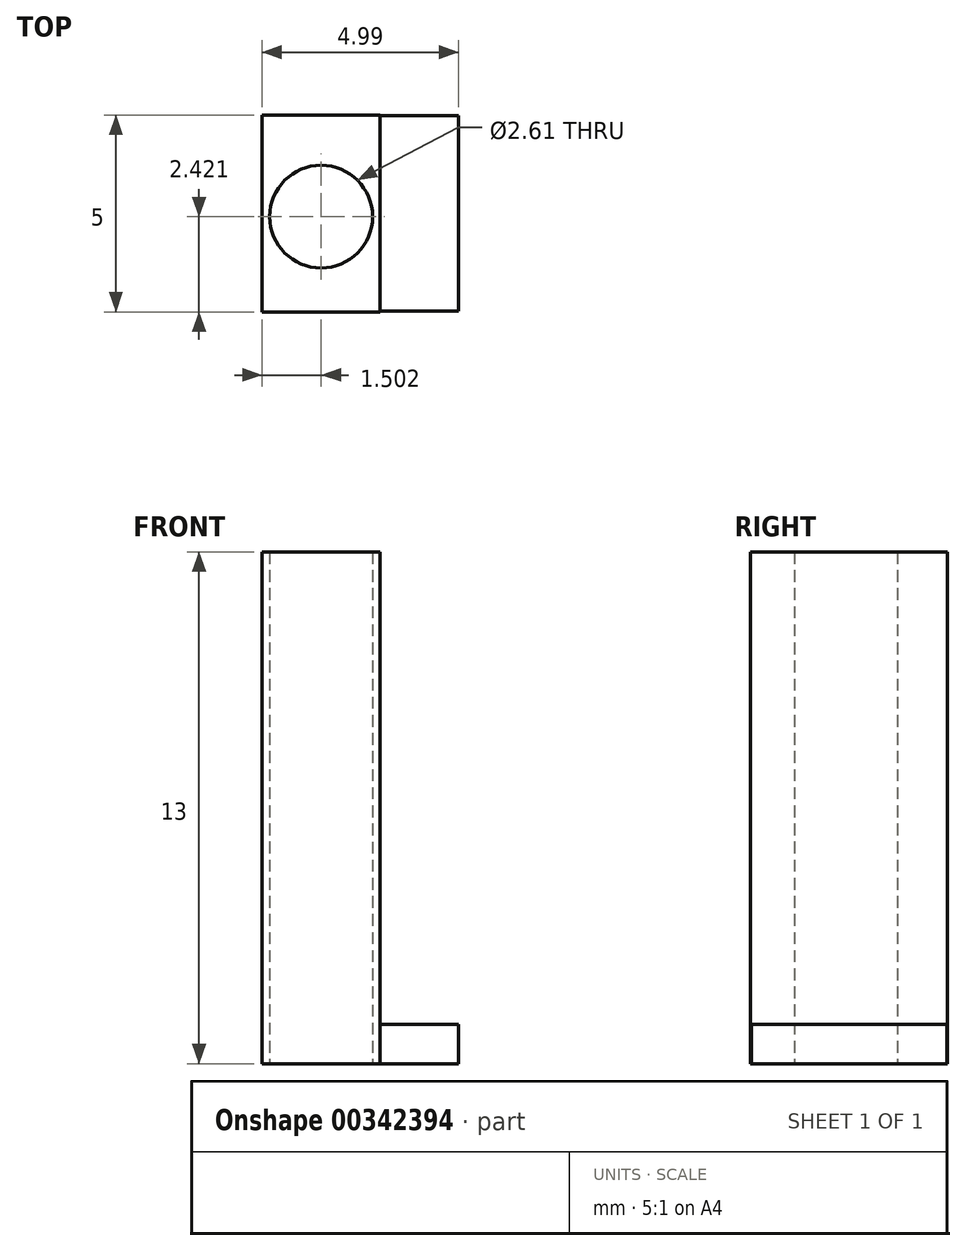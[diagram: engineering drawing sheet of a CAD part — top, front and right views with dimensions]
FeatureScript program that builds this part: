
annotation { "Feature Type Name" : "Feature", "Feature Type Description" : "" }
export const myFeature = defineFeature(function(context is Context, id is Id, definition is map)
    precondition{}
    {
        {
            var Q0;
            Q0=qCreatedBy(makeId("Top.planeOp"),FACE);
            var sketch = newSketch(context, id + "F0", { "sketchPlane" : qUnion([Q0])});
            skLineSegment(sketch, "E0.bottom", {"start": v(0, 2.2) * mm, "end": v(3, 2.2) * mm});
            skLineSegment(sketch, "E0.top", {"start": v(0, -2.8) * mm, "end": v(3, -2.8) * mm});
            skLineSegment(sketch, "E0.left", {"start": v(0, 2.2) * mm, "end": v(0, -2.8) * mm});
            skLineSegment(sketch, "E0.right", {"start": v(3, 2.2) * mm, "end": v(3, -2.8) * mm});
            skSolve(sketch);
        }
        {
            var Q0;
            Q0=makeQuery(id+"F0.imprint","IMPRINT",FACE,{"disambiguationData":[TD([[makeQuery(id+"F0.imprint","IMPRINT",EDGE,{"derivedFrom":sQuery(id+"F0.wireOp",EDGE,"E0.bottom")}),-1.0]])]});
            extrude(context, id + "F1", {"entities" : qUnion([Q0]), "depth" : 13 * mm});
        }
        {
            var Q0;
            Q0=makeQuery(id+"F1.opExtrude","SWEPT_FACE",FACE,{"disambiguationData":[OSD([sQuery(id+"F0.wireOp",EDGE,"E0.right")])]});
            cPlane(context, id + "F2", {"entities" : qUnion([Q0]), "cplaneType" : CPlaneType.OFFSET, "offset" : 0.01 * mm, "oppositeDirection" : true, "width" : 150 * mm, "height" : 150 * mm});
        }
        {
            var Q0;
            Q0=qCreatedBy(id+"F2.planeOp",FACE);
            var sketch = newSketch(context, id + "F3", { "sketchPlane" : qUnion([Q0])});
            skLineSegment(sketch, "E1.bottom", {"start": v(-2.77, 0) * mm, "end": v(2.19, 0) * mm});
            skLineSegment(sketch, "E1.top", {"start": v(-2.77, 1) * mm, "end": v(2.19, 1) * mm});
            skLineSegment(sketch, "E1.left", {"start": v(-2.77, 0) * mm, "end": v(-2.77, 1) * mm});
            skLineSegment(sketch, "E1.right", {"start": v(2.19, 0) * mm, "end": v(2.19, 1) * mm});
            skSolve(sketch);
        }
        {
            var Q0;
            Q0 = qSketchRegion(id + "F3", true);
            extrude(context, id + "F4", {"entities" : qUnion([Q0]), "depth" : 2 * mm});
        }
        {
            var Q0;
            Q0=qCreatedBy(makeId("Top.planeOp"),FACE);
            var sketch = newSketch(context, id + "F5", { "sketchPlane" : qUnion([Q0])});
            skCircle(sketch, "E2", {"center": v(1.5, -0.38) * mm, "radius": 1.3 * mm});
            skSolve(sketch);
        }
        {
            var Q0;
            Q0 = qSketchRegion(id + "F5", true);
            extrude(context, id + "F6", {"entities" : qUnion([Q0]), "operationType" : NewBodyOperationType.REMOVE, "depth" : 43.8 * mm});
        }
    });
